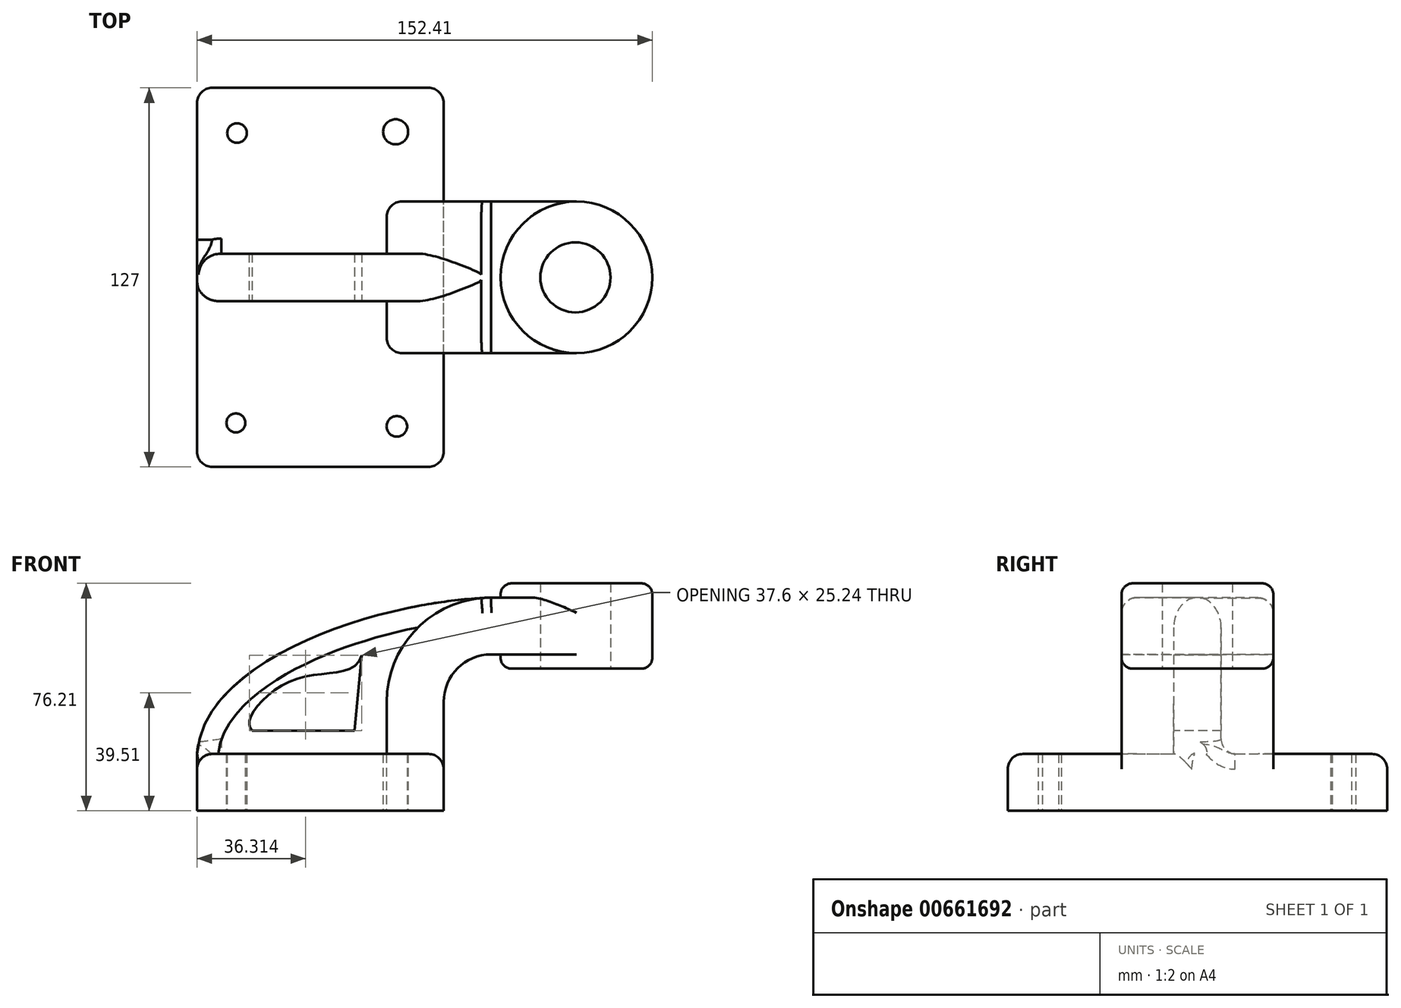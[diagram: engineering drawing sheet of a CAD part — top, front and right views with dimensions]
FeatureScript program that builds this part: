
annotation { "Feature Type Name" : "Feature", "Feature Type Description" : "" }
export const myFeature = defineFeature(function(context is Context, id is Id, definition is map)
    precondition{}
    {
        {
            var Q0;
            Q0=qCreatedBy(makeId("Front.planeOp"),FACE);
            var sketch = newSketch(context, id + "F0", { "sketchPlane" : qUnion([Q0])});
            skLineSegment(sketch, "E0.rect.bottom", {"start": v(-41.28, 9.52) * mm, "end": v(41.28, 9.52) * mm});
            skLineSegment(sketch, "E0.rect.top", {"start": v(-41.28, -9.52) * mm, "end": v(41.28, -9.52) * mm});
            skLineSegment(sketch, "E0.rect.left", {"start": v(-41.28, 9.52) * mm, "end": v(-41.28, -9.52) * mm});
            skLineSegment(sketch, "E0.rect.right", {"start": v(41.28, 9.52) * mm, "end": v(41.28, -9.52) * mm});
            skPoint(sketch, "E0.rect.middle", {"position": v(0, 0) * mm});
            skLineSegment(sketch, "E1", {"start": v(41.28, 9.52) * mm, "end": v(41.28, 27) * mm});
            skArc(sketch, "E2", {"start": v(41.28, 27) * mm, "mid": v(45.92, 38.23) * mm, "end": v(57.15, 42.88) * mm});
            skLineSegment(sketch, "E3", {"start": v(57.15, 42.88) * mm, "end": v(85.72, 42.88) * mm});
            skLineSegment(sketch, "E4.rect.bottom", {"start": v(60.32, 38.1) * mm, "end": v(111.12, 38.1) * mm});
            skLineSegment(sketch, "E4.rect.top", {"start": v(60.32, 66.68) * mm, "end": v(111.12, 66.68) * mm});
            skLineSegment(sketch, "E4.rect.left", {"start": v(60.32, 38.1) * mm, "end": v(60.32, 66.68) * mm});
            skLineSegment(sketch, "E4.rect.right", {"start": v(111.13, 38.1) * mm, "end": v(111.12, 66.68) * mm});
            skPoint(sketch, "E4.rect.middle", {"position": v(85.72, 52.39) * mm});
            skLineSegment(sketch, "E5.0", {"start": v(57.15, 61.93) * mm, "end": v(85.72, 61.93) * mm});
            skArc(sketch, "E5.1", {"start": v(22.23, 27) * mm, "mid": v(32.45, 51.7) * mm, "end": v(57.15, 61.93) * mm});
            skLineSegment(sketch, "E5.2", {"start": v(22.23, 9.52) * mm, "end": v(22.23, 27) * mm});
            skLineSegment(sketch, "E6", {"start": v(85.72, 38.1) * mm, "end": v(85.72, 66.68) * mm});
            skFitSpline(sketch, "E7", {"points": [v(-41.28, 9.53) * mm, v(57.15, 61.93) * mm], "startDerivative": vector(5.2, 92.34) * mm, "endDerivative": vector(120.92, 4.22) * mm});
            skSolve(sketch);
        }
        {
            var Q0;
            Q0=makeQuery(id+"F0.imprint","IMPRINT",FACE,{"disambiguationData":[TD([[makeQuery(id+"F0.imprint","IMPRINT",EDGE,{"derivedFrom":sQuery(id+"F0.wireOp",EDGE,"E0.rect.top")}),1.0]])]});
            extrude(context, id + "F1", {"entities" : qUnion([Q0]), "endBound" : BoundingType.SYMMETRIC, "depth" : 127 * mm});
        }
        {
            var Q0;
            {var subQ9=sQuery(id+"F0.wireOp",EDGE,"E1");Q0=makeQuery(id+"F0.imprint","IMPRINT",FACE,{"disambiguationData":[TD([[makeQuery(id+"F0.imprint","IMPRINT",EDGE,{"derivedFrom":subQ9}),1.0]])]});}
            var Q1;
            {var subQ0=sQuery(id+"F0.wireOp",EDGE,"E6");var subQ1=sQuery(id+"F0.wireOp",EDGE,"E3");var subQ2=makeQuery(id+"F0.imprint","INTERSECT",VERTEX,{"derivedFrom":[subQ1,subQ0]});Q1=makeQuery(id+"F0.imprint","IMPRINT",FACE,{"disambiguationData":[TD([[makeQuery(id+"F0.imprint","IMPRINT",EDGE,{"disambiguationData":[TD([[subQ2,1.0]])],"derivedFrom":subQ1}),1.0]])]});}
            extrude(context, id + "F2", {"entities" : qUnion([Q0, Q1]), "operationType" : NewBodyOperationType.ADD, "endBound" : BoundingType.SYMMETRIC, "depth" : 50.8 * mm});
        }
        {
            var Q0;
            {var subQ3=sQuery(id+"F0.wireOp",EDGE,"E5.2");Q0=makeQuery(id+"F0.imprint","IMPRINT",FACE,{"disambiguationData":[TD([[makeQuery(id+"F0.imprint","IMPRINT",EDGE,{"derivedFrom":subQ3}),1.0]])]});}
            extrude(context, id + "F3", {"entities" : qUnion([Q0]), "operationType" : NewBodyOperationType.ADD, "endBound" : BoundingType.SYMMETRIC, "depth" : 15.88 * mm});
        }
        {
            var Q0;
            {var subQ5=sQuery(id+"F0.wireOp",EDGE,"E4.rect.right");Q0=makeQuery(id+"F0.imprint","IMPRINT",FACE,{"disambiguationData":[TD([[makeQuery(id+"F0.imprint","IMPRINT",EDGE,{"derivedFrom":subQ5}),1.0]])]});}
            var Q1;
            Q1=sQuery(id+"F0.wireOp",EDGE,"E6");
            revolve(context, id + "F4", {"operationType" : NewBodyOperationType.ADD, "entities" : qUnion([Q0]), "axis" : qUnion([Q1]), "revolveType" : RevolveType.FULL});
        }
        {
            var Q0;
            Q0=makeQuery(id+"F1.opExtrude","CAP_EDGE",EDGE,{"disambiguationData":[OSD([sQuery(id+"F0.wireOp",EDGE,"E0.rect.right")])],"isStart":false});
            var Q1;
            Q1=makeQuery(id+"F1.opExtrude","CAP_EDGE",EDGE,{"disambiguationData":[OSD([sQuery(id+"F0.wireOp",EDGE,"E0.rect.left")])],"isStart":false});
            var Q2;
            Q2=makeQuery(id+"F1.opExtrude","CAP_EDGE",EDGE,{"disambiguationData":[OSD([sQuery(id+"F0.wireOp",EDGE,"E0.rect.right")])],"isStart":true});
            var Q3;
            Q3=makeQuery(id+"F1.opExtrude","CAP_EDGE",EDGE,{"disambiguationData":[OSD([sQuery(id+"F0.wireOp",EDGE,"E0.rect.left")])],"isStart":true});
            fillet(context, id + "F5", {"entities" : qUnion([Q0, Q1, Q2, Q3]), "radius" : 5.08 * mm, "tangentPropagation" : true, "allowEdgeOverflow" : false});
        }
        {
            var Q0;
            Q0=makeQuery(id+"F4.opRevolve","SWEPT_EDGE",EDGE,{"disambiguationData":[OSD([sQuery(id+"F0.wireOp",EDGE,"E4.rect.top"),sQuery(id+"F0.wireOp",EDGE,"E4.rect.right")])]});
            var Q1;
            Q1=makeQuery(id+"F4.opRevolve","SWEPT_EDGE",EDGE,{"disambiguationData":[OSD([sQuery(id+"F0.wireOp",EDGE,"E4.rect.bottom"),sQuery(id+"F0.wireOp",EDGE,"E4.rect.right")])]});
            fillet(context, id + "F6", {"entities" : qUnion([Q0, Q1]), "radius" : 3.7 * mm, "tangentPropagation" : true, "allowEdgeOverflow" : false});
        }
        {
            var Q0;
            Q0=makeQuery(id+"F3.opExtrude","CAP_EDGE",EDGE,{"disambiguationData":[OSD([sQuery(id+"F0.wireOp",EDGE,"E7")])],"isStart":true});
            var Q1;
            Q1=makeQuery(id+"F3.opExtrude","CAP_EDGE",EDGE,{"disambiguationData":[OSD([sQuery(id+"F0.wireOp",EDGE,"E7")])],"isStart":false});
            fillet(context, id + "F7", {"entities" : qUnion([Q0, Q1]), "radius" : 7.06 * mm, "tangentPropagation" : true, "allowEdgeOverflow" : false});
        }
        {
            var Q0;
            Q0=makeQuery(id+"F3.opExtrude","CAP_EDGE",EDGE,{"disambiguationData":[OSD([sQuery(id+"F0.wireOp",EDGE,"E0.rect.bottom")])],"isStart":true});
            var Q1;
            Q1=makeQuery(id+"F3.opExtrude","CAP_EDGE",EDGE,{"disambiguationData":[OSD([sQuery(id+"F0.wireOp",EDGE,"E0.rect.bottom")])],"isStart":false});
            fillet(context, id + "F8", {"entities" : qUnion([Q0, Q1]), "radius" : 5.08 * mm, "tangentPropagation" : true, "allowEdgeOverflow" : false});
        }
        {
            var Q0;
            Q0=makeQuery(id+"F2.opExtrude","CAP_EDGE",EDGE,{"disambiguationData":[OSD([sQuery(id+"F0.wireOp",EDGE,"E5.0")])],"isStart":true});
            var Q1;
            Q1=makeQuery(id+"F2.opExtrude","CAP_EDGE",EDGE,{"disambiguationData":[OSD([sQuery(id+"F0.wireOp",EDGE,"E5.0")])],"isStart":false});
            var Q2;
            Q2=makeQuery(id+"F2.opExtrude","CAP_EDGE",EDGE,{"disambiguationData":[OSD([sQuery(id+"F0.wireOp",EDGE,"E0.rect.bottom")])],"isStart":false});
            var Q3;
            Q3=makeQuery(id+"F2.opExtrude","CAP_EDGE",EDGE,{"disambiguationData":[OSD([sQuery(id+"F0.wireOp",EDGE,"E5.1")])],"isStart":false});
            var Q4;
            Q4=makeQuery(id+"F2.opExtrude","CAP_EDGE",EDGE,{"disambiguationData":[OSD([sQuery(id+"F0.wireOp",EDGE,"E0.rect.bottom")])],"isStart":true});
            var Q5;
            Q5=makeQuery(id+"F2.opExtrude","CAP_EDGE",EDGE,{"disambiguationData":[OSD([sQuery(id+"F0.wireOp",EDGE,"E5.1")])],"isStart":true});
            fillet(context, id + "F9", {"entities" : qUnion([Q0, Q1, Q2, Q3, Q4, Q5]), "radius" : 5.08 * mm, "tangentPropagation" : true, "allowEdgeOverflow" : false});
        }
        {
            var Q0;
            Q0=makeQuery(id+"F1.opExtrude","CAP_EDGE",EDGE,{"disambiguationData":[OSD([sQuery(id+"F0.wireOp",EDGE,"E0.rect.bottom")])],"isStart":false});
            var Q1;
            Q1=makeQuery(id+"F1.opExtrude","CAP_EDGE",EDGE,{"disambiguationData":[OSD([sQuery(id+"F0.wireOp",EDGE,"E0.rect.bottom")])],"isStart":true});
            fillet(context, id + "F10", {"entities" : qUnion([Q0, Q1]), "radius" : 5.08 * mm, "tangentPropagation" : true, "allowEdgeOverflow" : false});
        }
        {
            var Q0;
            Q0=qCreatedBy(makeId("Top.planeOp"),FACE);
            var sketch = newSketch(context, id + "F11", { "sketchPlane" : qUnion([Q0])});
            skCircle(sketch, "E8", {"center": v(85.39, 0) * mm, "radius": 11.73 * mm});
            skSolve(sketch);
        }
        {
            var Q0;
            Q0=makeQuery(id+"F11.imprint","IMPRINT",FACE,{"disambiguationData":[TD([[makeQuery(id+"F11.imprint","IMPRINT",EDGE,{"derivedFrom":sQuery(id+"F11.wireOp",EDGE,"E8")}),1.0]])]});
            extrude(context, id + "F12", {"entities" : qUnion([Q0]), "operationType" : NewBodyOperationType.REMOVE, "depth" : 123.24 * mm, "offsetDistance" : 25.4 * mm});
        }
        {
            var Q0;
            Q0=qCreatedBy(makeId("Top.planeOp"),FACE);
            var sketch = newSketch(context, id + "F13", { "sketchPlane" : qUnion([Q0])});
            skCircle(sketch, "E9", {"center": v(-27.9, 48.35) * mm, "radius": 3.29 * mm});
            skCircle(sketch, "E10", {"center": v(25.2, 48.76) * mm, "radius": 4.2 * mm});
            skCircle(sketch, "E11", {"center": v(-28.27, -48.75) * mm, "radius": 3.18 * mm});
            skCircle(sketch, "E12", {"center": v(25.6, -49.92) * mm, "radius": 3.45 * mm});
            skSolve(sketch);
        }
        {
            var Q0;
            Q0 = qSketchRegion(id + "F13", true);
            extrude(context, id + "F14", {"entities" : qUnion([Q0]), "operationType" : NewBodyOperationType.REMOVE, "endBound" : BoundingType.SYMMETRIC, "depth" : 25.4 * mm, "offsetDistance" : 25.4 * mm});
        }
        {
            var Q0;
            Q0=qCreatedBy(makeId("Front.planeOp"),FACE);
            var sketch = newSketch(context, id + "F15", { "sketchPlane" : qUnion([Q0])});
            skFitSpline(sketch, "E13", {"points": [v(13.84, 42.6) * mm, v(-7.36, 34.9) * mm, v(-23.84, 19.78) * mm, v(-22.83, 17.36) * mm, v(-23.84, 18.1) * mm], "startDerivative": vector(-18.2, -59.38) * mm, "endDerivative": vector(-16.42, 12.84) * mm});
            skLineSegment(sketch, "E14", {"start": v(-22.83, 17.36) * mm, "end": v(11.48, 17.36) * mm});
            skLineSegment(sketch, "E15", {"start": v(13.84, 42.6) * mm, "end": v(11.48, 17.36) * mm});
            skSolve(sketch);
        }
        {
            var Q0;
            Q0 = qSketchRegion(id + "F15", true);
            extrude(context, id + "F16", {"entities" : qUnion([Q0]), "operationType" : NewBodyOperationType.REMOVE, "endBound" : BoundingType.SYMMETRIC, "oppositeDirection" : true, "depth" : 157.82 * mm, "offsetDistance" : 25.4 * mm});
        }
    });
